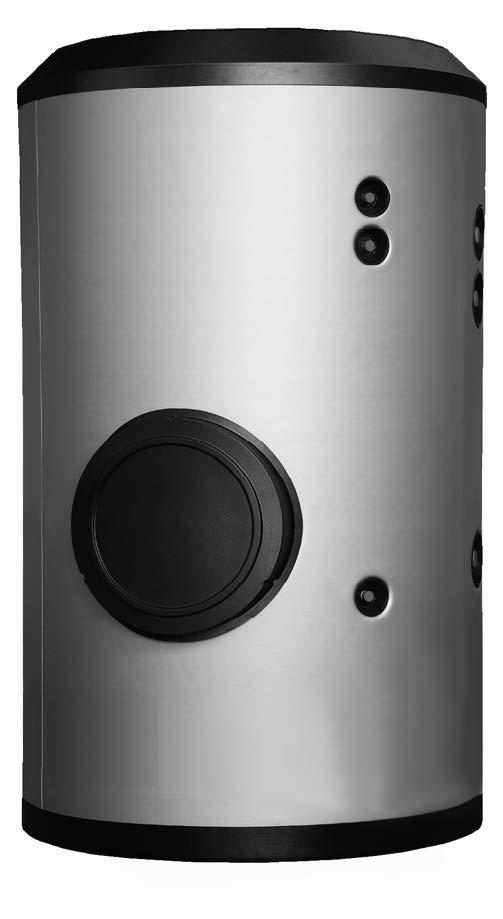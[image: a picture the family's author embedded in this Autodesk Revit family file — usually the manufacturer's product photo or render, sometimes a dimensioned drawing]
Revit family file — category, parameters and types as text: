
# Revit family: IMXV-2000SSB_CC01865
name_source: partatom
category: Aparatos eléctricos
revit_build: Autodesk Revit 2016 (Build: 20150220_1215(x64)
units: mm (PartAtom-declared; Revit-internal decimal feet)

## family parameters
Compartido = No
Corte con vacíos al cargar = No
Número OmniClass = 23.80.00.00
Punto de cálculo de habitación = No
Se basa en plano de trabajo = No
Siempre vertical = Sí
Título OmniClass = Electric Power and Lighting

## types (1)
- Depósitos gran capacidad IMXV-SB
    Clase eficiencia energética = C
    Costo = 0 $
    Código de montaje = CC01865
    Descripción = DEPÓSITOS GRAN CAPACIDAD VITRIFICADOS ACERO INOX.
    Dimensiones = 1360 x 2280 mm
    Fabricante = SALVADOR ESCODA
    Imagen de tipo = RB-IMXV.jpg
    Modelo = IMXV 2000 SSB
    Peso en vacío = 363 Kg
    Presión máx. circuito = 25 bar
    Presión máx. depósito = 8 bar
    Superfície intercambio = 5 m2
    Temperatura máx. ACS = 90 ºC
    Temperatura máx. circuito = 120 ºC
    URL = www.salvadorescoda.com
    Volúmen = 2000 l
